FCSTD DOCUMENT  (FreeCAD 0.22R37926 (Git))
Label: pmpd_02
License: All rights reserved
LicenseURL: http://en.wikipedia.org/wiki/All_rights_reserved
objects: Part::Vertex×50, App::FeaturePython×1
note: 50 computed .brp shape members not serialized (recipe doc carries the construction recipe); baked Part::Feature solids carry a one-line shape summary decoded from their .brp

FEATURE [App::FeaturePython] PDInclude  # WARN: FeaturePython — macro-defined, semantics opaque (R4)
FEATURE [Part::Vertex] Vertex  label="pt0"
  AttacherType = Attacher::AttachEngine3D
  X = 0
  Y = 0
  Z = 0
FEATURE [Part::Vertex] Vertex001  label="pt1"
  AttacherType = Attacher::AttachEngine3D
  Placement = pos=(-0.00483521,19.9399,4.94431) rot=(0,0,1;0rad)
  X = 0
  Y = 0
  Z = 0
FEATURE [Part::Vertex] Vertex002  label="pt2"
  AttacherType = Attacher::AttachEngine3D
  Placement = pos=(0.0269032,39.9247,7.78191) rot=(0,0,1;0rad)
  X = 0
  Y = 0
  Z = 0
FEATURE [Part::Vertex] Vertex003  label="pt3"
  AttacherType = Attacher::AttachEngine3D
  Placement = pos=(0.00677503,59.9188,3.50659) rot=(0,0,1;0rad)
  X = 0
  Y = 0
  Z = 0
FEATURE [Part::Vertex] Vertex004  label="pt4"
  AttacherType = Attacher::AttachEngine3D
  Placement = pos=(0,80,0) rot=(0,0,1;0rad)
  X = 0
  Y = 0
  Z = 0
FEATURE [Part::Vertex] Vertex005  label="pt5"
  AttacherType = Attacher::AttachEngine3D
  Placement = pos=(9.95618,-0.0227379,6.24158) rot=(0,0,1;0rad)
  X = 0
  Y = 0
  Z = 0
FEATURE [Part::Vertex] Vertex006  label="pt6"
  AttacherType = Attacher::AttachEngine3D
  Placement = pos=(10.0231,19.9074,7.06106) rot=(0,0,1;0rad)
  X = 0
  Y = 0
  Z = 0
FEATURE [Part::Vertex] Vertex007  label="pt7"
  AttacherType = Attacher::AttachEngine3D
  Placement = pos=(9.98394,39.9369,6.51078) rot=(0,0,1;0rad)
  X = 0
  Y = 0
  Z = 0
FEATURE [Part::Vertex] Vertex008  label="pt8"
  AttacherType = Attacher::AttachEngine3D
  Placement = pos=(9.94818,59.941,7.23965) rot=(0,0,1;0rad)
  X = 0
  Y = 0
  Z = 0
FEATURE [Part::Vertex] Vertex009  label="pt9"
  AttacherType = Attacher::AttachEngine3D
  Placement = pos=(9.87252,79.8999,5.45104) rot=(0,0,1;0rad)
  X = 0
  Y = 0
  Z = 0
FEATURE [Part::Vertex] Vertex010  label="pt10"
  AttacherType = Attacher::AttachEngine3D
  Placement = pos=(19.9795,-0.0186856,4.9738) rot=(0,0,1;0rad)
  X = 0
  Y = 0
  Z = 0
FEATURE [Part::Vertex] Vertex011  label="pt11"
  AttacherType = Attacher::AttachEngine3D
  Placement = pos=(19.9796,19.9697,5.25625) rot=(0,0,1;0rad)
  X = 0
  Y = 0
  Z = 0
FEATURE [Part::Vertex] Vertex012  label="pt12"
  AttacherType = Attacher::AttachEngine3D
  Placement = pos=(20.0438,39.9245,8.25452) rot=(0,0,1;0rad)
  X = 0
  Y = 0
  Z = 0
FEATURE [Part::Vertex] Vertex013  label="pt13"
  AttacherType = Attacher::AttachEngine3D
  Placement = pos=(19.9268,59.9421,5.03227) rot=(0,0,1;0rad)
  X = 0
  Y = 0
  Z = 0
FEATURE [Part::Vertex] Vertex014  label="pt14"
  AttacherType = Attacher::AttachEngine3D
  Placement = pos=(19.898,79.8393,8.38477) rot=(0,0,1;0rad)
  X = 0
  Y = 0
  Z = 0
FEATURE [Part::Vertex] Vertex015  label="pt15"
  AttacherType = Attacher::AttachEngine3D
  Placement = pos=(30.0629,-0.014368,7.13974) rot=(0,0,1;0rad)
  X = 0
  Y = 0
  Z = 0
FEATURE [Part::Vertex] Vertex016  label="pt16"
  AttacherType = Attacher::AttachEngine3D
  Placement = pos=(30.0195,19.9562,6.45888) rot=(0,0,1;0rad)
  X = 0
  Y = 0
  Z = 0
FEATURE [Part::Vertex] Vertex017  label="pt17"
  AttacherType = Attacher::AttachEngine3D
  Placement = pos=(30.0505,39.9333,7.91071) rot=(0,0,1;0rad)
  X = 0
  Y = 0
  Z = 0
FEATURE [Part::Vertex] Vertex018  label="pt18"
  AttacherType = Attacher::AttachEngine3D
  Placement = pos=(29.9597,59.9384,7.02083) rot=(0,0,1;0rad)
  X = 0
  Y = 0
  Z = 0
FEATURE [Part::Vertex] Vertex019  label="pt19"
  AttacherType = Attacher::AttachEngine3D
  Placement = pos=(29.9735,79.8367,8.78327) rot=(0,0,1;0rad)
  X = 0
  Y = 0
  Z = 0
FEATURE [Part::Vertex] Vertex020  label="pt20"
  AttacherType = Attacher::AttachEngine3D
  Placement = pos=(40.0266,-0.00961545,5.4229) rot=(0,0,1;0rad)
  X = 0
  Y = 0
  Z = 0
FEATURE [Part::Vertex] Vertex021  label="pt21"
  AttacherType = Attacher::AttachEngine3D
  Placement = pos=(40.0975,19.9612,7.49799) rot=(0,0,1;0rad)
  X = 0
  Y = 0
  Z = 0
FEATURE [Part::Vertex] Vertex022  label="pt22"
  AttacherType = Attacher::AttachEngine3D
  Placement = pos=(40,40,10) rot=(0,0,1;0rad)
  X = 0
  Y = 0
  Z = 0
FEATURE [Part::Vertex] Vertex023  label="pt23"
  AttacherType = Attacher::AttachEngine3D
  Placement = pos=(39.9439,59.955,6.07505) rot=(0,0,1;0rad)
  X = 0
  Y = 0
  Z = 0
FEATURE [Part::Vertex] Vertex024  label="pt24"
  AttacherType = Attacher::AttachEngine3D
  Placement = pos=(39.9886,79.9011,7.71315) rot=(0,0,1;0rad)
  X = 0
  Y = 0
  Z = 0
FEATURE [Part::Vertex] Vertex025  label="pt25"
  AttacherType = Attacher::AttachEngine3D
  Placement = pos=(50.0609,0.0102146,5.15164) rot=(0,0,1;0rad)
  X = 0
  Y = 0
  Z = 0
FEATURE [Part::Vertex] Vertex026  label="pt26"
  AttacherType = Attacher::AttachEngine3D
  Placement = pos=(49.8936,20.048,3.69607) rot=(0,0,1;0rad)
  X = 0
  Y = 0
  Z = 0
FEATURE [Part::Vertex] Vertex027  label="pt27"
  AttacherType = Attacher::AttachEngine3D
  Placement = pos=(50.0286,39.9615,7.07475) rot=(0,0,1;0rad)
  X = 0
  Y = 0
  Z = 0
FEATURE [Part::Vertex] Vertex028  label="pt28"
  AttacherType = Attacher::AttachEngine3D
  Placement = pos=(49.9584,59.9675,5.87896) rot=(0,0,1;0rad)
  X = 0
  Y = 0
  Z = 0
FEATURE [Part::Vertex] Vertex029  label="pt29"
  AttacherType = Attacher::AttachEngine3D
  Placement = pos=(49.8577,79.9725,4.87832) rot=(0,0,1;0rad)
  X = 0
  Y = 0
  Z = 0
FEATURE [Part::Vertex] Vertex030  label="pt30"
  AttacherType = Attacher::AttachEngine3D
  Placement = pos=(59.7142,0.229598,0.41296) rot=(0,0,1;0rad)
  X = 0
  Y = 0
  Z = 0
FEATURE [Part::Vertex] Vertex031  label="pt31"
  AttacherType = Attacher::AttachEngine3D
  Placement = pos=(60.0429,19.9754,6.30209) rot=(0,0,1;0rad)
  X = 0
  Y = 0
  Z = 0
FEATURE [Part::Vertex] Vertex032  label="pt32"
  AttacherType = Attacher::AttachEngine3D
  Placement = pos=(60.0242,39.9801,6.62095) rot=(0,0,1;0rad)
  X = 0
  Y = 0
  Z = 0
FEATURE [Part::Vertex] Vertex033  label="pt33"
  AttacherType = Attacher::AttachEngine3D
  Placement = pos=(59.8063,59.9899,3.35541) rot=(0,0,1;0rad)
  X = 0
  Y = 0
  Z = 0
FEATURE [Part::Vertex] Vertex034  label="pt34"
  AttacherType = Attacher::AttachEngine3D
  Placement = pos=(59.9345,79.965,5.61693) rot=(0,0,1;0rad)
  X = 0
  Y = 0
  Z = 0
FEATURE [Part::Vertex] Vertex035  label="pt35"
  AttacherType = Attacher::AttachEngine3D
  Placement = pos=(69.8955,0.0698736,2.51869) rot=(0,0,1;0rad)
  X = 0
  Y = 0
  Z = 0
FEATURE [Part::Vertex] Vertex036  label="pt36"
  AttacherType = Attacher::AttachEngine3D
  Placement = pos=(69.9844,19.9997,4.66392) rot=(0,0,1;0rad)
  X = 0
  Y = 0
  Z = 0
FEATURE [Part::Vertex] Vertex037  label="pt37"
  AttacherType = Attacher::AttachEngine3D
  Placement = pos=(69.8678,40.0231,3.7204) rot=(0,0,1;0rad)
  X = 0
  Y = 0
  Z = 0
FEATURE [Part::Vertex] Vertex038  label="pt38"
  AttacherType = Attacher::AttachEngine3D
  Placement = pos=(69.6396,59.9838,1.00562) rot=(0,0,1;0rad)
  X = 0
  Y = 0
  Z = 0
FEATURE [Part::Vertex] Vertex039  label="pt39"
  AttacherType = Attacher::AttachEngine3D
  Placement = pos=(69.9942,79.9326,5.90549) rot=(0,0,1;0rad)
  X = 0
  Y = 0
  Z = 0
FEATURE [Part::Vertex] Vertex040  label="pt40"
  AttacherType = Attacher::AttachEngine3D
  Placement = pos=(80,0,0) rot=(0,0,1;0rad)
  X = 0
  Y = 0
  Z = 0
FEATURE [Part::Vertex] Vertex041  label="pt41"
  AttacherType = Attacher::AttachEngine3D
  Placement = pos=(79.6205,20.1654,0.0042347) rot=(0,0,1;0rad)
  X = 0
  Y = 0
  Z = 0
FEATURE [Part::Vertex] Vertex042  label="pt42"
  AttacherType = Attacher::AttachEngine3D
  Placement = pos=(79.9134,40.0195,4.2954) rot=(0,0,1;0rad)
  X = 0
  Y = 0
  Z = 0
FEATURE [Part::Vertex] Vertex043  label="pt43"
  AttacherType = Attacher::AttachEngine3D
  Placement = pos=(79.8728,60.0441,4.43466) rot=(0,0,1;0rad)
  X = 0
  Y = 0
  Z = 0
FEATURE [Part::Vertex] Vertex044  label="pt44"
  AttacherType = Attacher::AttachEngine3D
  Placement = pos=(79.6887,80.0175,1.71075) rot=(0,0,1;0rad)
  X = 0
  Y = 0
  Z = 0
FEATURE [Part::Vertex] Vertex045  label="pt45"
  AttacherType = Attacher::AttachEngine3D
  Placement = pos=(89.8045,0.12721,0.509232) rot=(0,0,1;0rad)
  X = 0
  Y = 0
  Z = 0
FEATURE [Part::Vertex] Vertex046  label="pt46"
  AttacherType = Attacher::AttachEngine3D
  Placement = pos=(89.8216,20.0766,1.77397) rot=(0,0,1;0rad)
  X = 0
  Y = 0
  Z = 0
FEATURE [Part::Vertex] Vertex047  label="pt47"
  AttacherType = Attacher::AttachEngine3D
  Placement = pos=(89.9084,40.0253,4.06321) rot=(0,0,1;0rad)
  X = 0
  Y = 0
  Z = 0
FEATURE [Part::Vertex] Vertex048  label="pt48"
  AttacherType = Attacher::AttachEngine3D
  Placement = pos=(89.8469,60.0628,3.44982) rot=(0,0,1;0rad)
  X = 0
  Y = 0
  Z = 0
FEATURE [Part::Vertex] Vertex049  label="pt49"
  AttacherType = Attacher::AttachEngine3D
  Placement = pos=(90,80,0) rot=(0,0,1;0rad)
  X = 0
  Y = 0
  Z = 0
